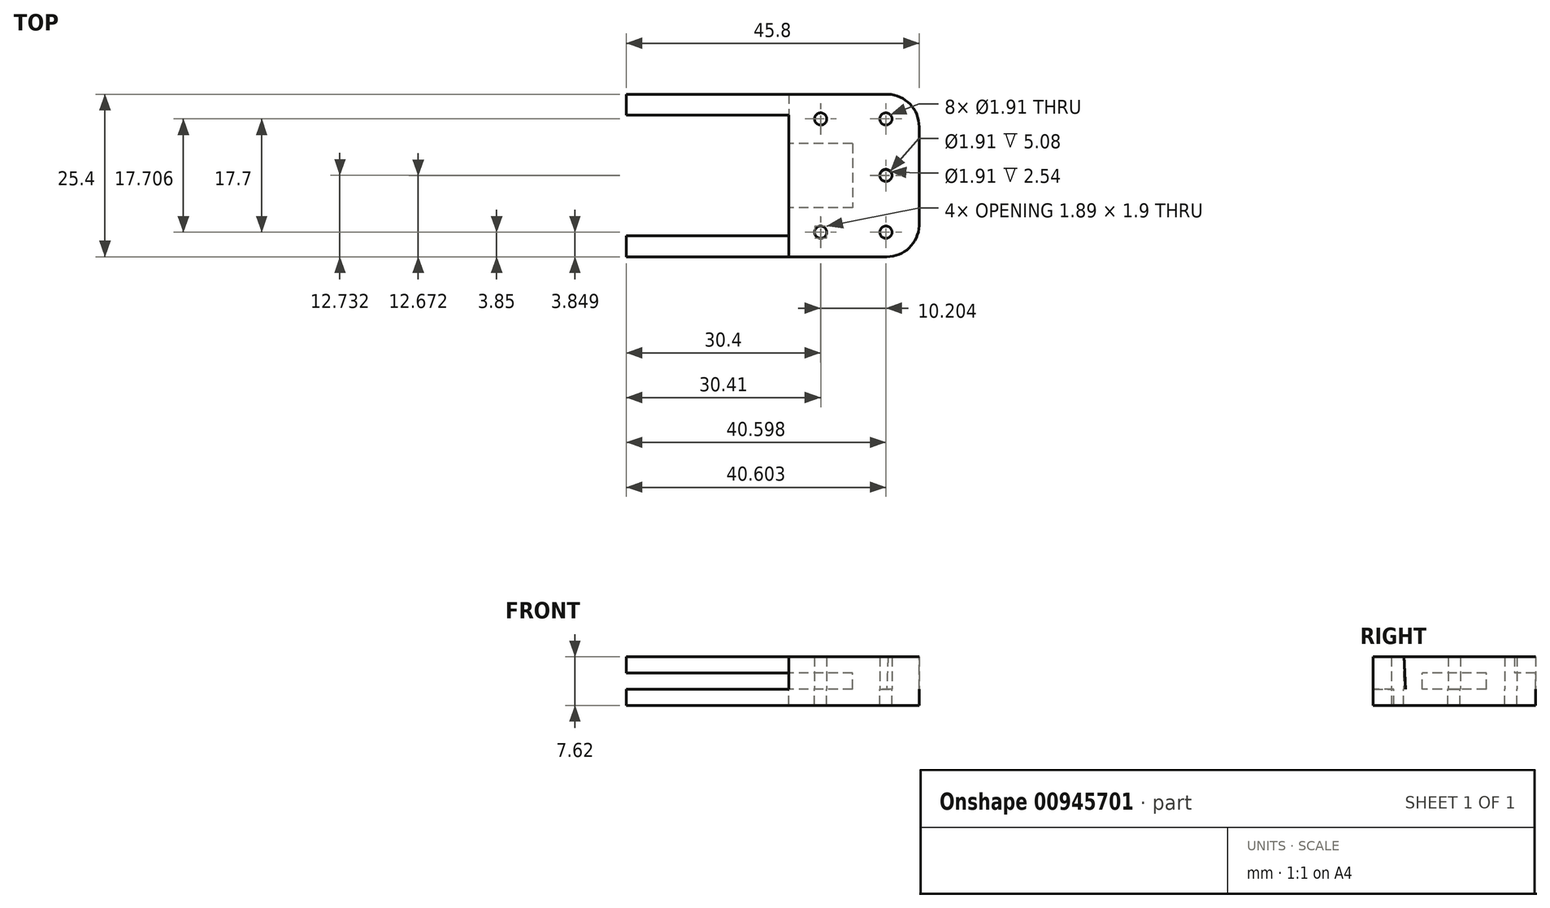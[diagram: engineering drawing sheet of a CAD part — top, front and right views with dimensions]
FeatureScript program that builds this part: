
annotation { "Feature Type Name" : "Feature", "Feature Type Description" : "" }
export const myFeature = defineFeature(function(context is Context, id is Id, definition is map)
    precondition{}
    {
        {
            var Q0;
            Q0=qCreatedBy(makeId("Top.planeOp"),FACE);
            var sketch = newSketch(context, id + "F0", { "sketchPlane" : qUnion([Q0])});
            skLineSegment(sketch, "E0.bottom", {"start": v(0, 0) * mm, "end": v(20.4, 0) * mm});
            skLineSegment(sketch, "E0.top", {"start": v(0, -25.4) * mm, "end": v(20.4, -25.4) * mm});
            skLineSegment(sketch, "E0.left", {"start": v(0, 0) * mm, "end": v(0, -25.4) * mm});
            skLineSegment(sketch, "E0.right", {"start": v(20.4, 0) * mm, "end": v(20.4, -25.4) * mm});
            skLineSegment(sketch, "E1.bottom", {"start": v(0, 0) * mm, "end": v(-25.4, 0) * mm});
            skLineSegment(sketch, "E1.top", {"start": v(0, -3.27) * mm, "end": v(-25.4, -3.27) * mm});
            skLineSegment(sketch, "E1.left", {"start": v(0, 0) * mm, "end": v(0, -3.27) * mm});
            skLineSegment(sketch, "E1.right", {"start": v(-25.4, 0) * mm, "end": v(-25.4, -3.27) * mm});
            skLineSegment(sketch, "E2.bottom", {"start": v(0, -7.7) * mm, "end": v(10, -7.7) * mm});
            skLineSegment(sketch, "E2.top", {"start": v(0, -17.7) * mm, "end": v(10, -17.7) * mm});
            skLineSegment(sketch, "E2.right", {"start": v(10, -7.7) * mm, "end": v(10, -17.7) * mm});
            skCircle(sketch, "E3", {"center": v(5, -3.85) * mm, "radius": 0.95 * mm});
            skCircle(sketch, "E4", {"center": v(15.2, -3.85) * mm, "radius": 0.95 * mm});
            skCircle(sketch, "E5", {"center": v(15.2, -21.55) * mm, "radius": 0.95 * mm});
            skCircle(sketch, "E6", {"center": v(5, -21.55) * mm, "radius": 0.95 * mm});
            skCircle(sketch, "E7", {"center": v(15.2, -12.67) * mm, "radius": 0.95 * mm});
            skSolve(sketch);
        }
        {
            var Q0;
            Q0=makeQuery(id+"F0.imprint","IMPRINT",FACE,{"disambiguationData":[TD([[makeQuery(id+"F0.imprint","IMPRINT",EDGE,{"derivedFrom":sQuery(id+"F0.wireOp",EDGE,"E1.bottom")}),1.0]])]});
            var Q1;
            Q1=makeQuery(id+"F0.imprint","IMPRINT",FACE,{"disambiguationData":[TD([[makeQuery(id+"F0.imprint","IMPRINT",EDGE,{"derivedFrom":sQuery(id+"F0.wireOp",EDGE,"E2.bottom")}),-1.0]])]});
            var Q2;
            Q2=makeQuery(id+"F0.imprint","IMPRINT",FACE,{"disambiguationData":[TD([[makeQuery(id+"F0.imprint","IMPRINT",EDGE,{"derivedFrom":sQuery(id+"F0.wireOp",EDGE,"E0.bottom")}),-1.0]])]});
            extrude(context, id + "F1", {"entities" : qUnion([Q0, Q1, Q2]), "depth" : 2.54 * mm, "offsetDistance" : 25.4 * mm});
        }
        {
            var Q0;
            Q0=qCreatedBy(makeId("Top.planeOp"),FACE);
            var sketch = newSketch(context, id + "F2", { "sketchPlane" : qUnion([Q0])});
            skLineSegment(sketch, "E8.bottom", {"start": v(0, 0) * mm, "end": v(20.4, 0) * mm});
            skLineSegment(sketch, "E8.top", {"start": v(0, -25.4) * mm, "end": v(20.4, -25.4) * mm});
            skLineSegment(sketch, "E8.right", {"start": v(20.4, 0) * mm, "end": v(20.4, -25.4) * mm});
            skLineSegment(sketch, "E9.bottom", {"start": v(10, -7.7) * mm, "end": v(0, -7.7) * mm});
            skLineSegment(sketch, "E9.top", {"start": v(10, -17.7) * mm, "end": v(0, -17.7) * mm});
            skLineSegment(sketch, "E9.left", {"start": v(10, -7.7) * mm, "end": v(10, -17.7) * mm});
            skLineSegment(sketch, "E10", {"start": v(0, 0) * mm, "end": v(0, -7.7) * mm});
            skLineSegment(sketch, "E11", {"start": v(0, -25.4) * mm, "end": v(0, -17.7) * mm});
            skCircle(sketch, "E12", {"center": v(5, -3.85) * mm, "radius": 0.95 * mm});
            skCircle(sketch, "E13", {"center": v(15.2, -3.85) * mm, "radius": 0.95 * mm});
            skCircle(sketch, "E14", {"center": v(15.2, -21.55) * mm, "radius": 0.95 * mm});
            skCircle(sketch, "E15", {"center": v(5, -21.55) * mm, "radius": 0.95 * mm});
            skCircle(sketch, "E16", {"center": v(15.2, -12.67) * mm, "radius": 0.95 * mm});
            skSolve(sketch);
        }
        {
            var Q0;
            Q0 = qSketchRegion(id + "F2", true);
            extrude(context, id + "F3", {"entities" : qUnion([Q0]), "operationType" : NewBodyOperationType.ADD, "oppositeDirection" : true, "depth" : 2.54 * mm, "offsetDistance" : 25.4 * mm});
        }
        {
            var Q0;
            Q0=makeQuery(id+"F3.boolean.opBoolean","MERGE",EDGE,{"derivedFrom":[makeQuery(id+"F1.opExtrude","SWEPT_EDGE",EDGE,{"disambiguationData":[OSD([sQuery(id+"F0.wireOp",EDGE,"E0.top"),sQuery(id+"F0.wireOp",EDGE,"E0.right")])]}),makeQuery(id+"F3.opExtrude","SWEPT_EDGE",EDGE,{"disambiguationData":[OSD([sQuery(id+"F2.wireOp",EDGE,"E8.top"),sQuery(id+"F2.wireOp",EDGE,"E8.right")])]})]});
            var Q1;
            Q1=makeQuery(id+"F3.boolean.opBoolean","MERGE",EDGE,{"derivedFrom":[makeQuery(id+"F1.opExtrude","SWEPT_EDGE",EDGE,{"disambiguationData":[OSD([sQuery(id+"F0.wireOp",EDGE,"E0.bottom"),sQuery(id+"F0.wireOp",EDGE,"E0.right")])]}),makeQuery(id+"F3.opExtrude","SWEPT_EDGE",EDGE,{"disambiguationData":[OSD([sQuery(id+"F2.wireOp",EDGE,"E8.bottom"),sQuery(id+"F2.wireOp",EDGE,"E8.right")])]})]});
            fillet(context, id + "F4", {"entities" : qUnion([Q0, Q1]), "radius" : 2.54 * mm, "tangentPropagation" : true, "allowEdgeOverflow" : false});
        }
        {
            var Q0;
            Q0=makeQuery(id+"F3.opExtrude","CAP_FACE",FACE,{"disambiguationData":[OSD([sQuery(id+"F2.wireOp",EDGE,"E8.bottom"),sQuery(id+"F2.wireOp",EDGE,"E8.top"),sQuery(id+"F2.wireOp",EDGE,"E8.right"),sQuery(id+"F2.wireOp",EDGE,"E9.bottom"),sQuery(id+"F2.wireOp",EDGE,"E9.top"),sQuery(id+"F2.wireOp",EDGE,"E9.left"),sQuery(id+"F2.wireOp",EDGE,"E10"),sQuery(id+"F2.wireOp",EDGE,"E11"),sQuery(id+"F2.wireOp",EDGE,"E12"),sQuery(id+"F2.wireOp",EDGE,"E13"),sQuery(id+"F2.wireOp",EDGE,"E14"),sQuery(id+"F2.wireOp",EDGE,"E15"),sQuery(id+"F2.wireOp",EDGE,"E16")])],"isStart":false});
            var sketch = newSketch(context, id + "F5", { "sketchPlane" : qUnion([Q0])});
            skLineSegment(sketch, "E17.bottom", {"start": v(0, 25.4) * mm, "end": v(20.4, 25.4) * mm});
            skLineSegment(sketch, "E17.top", {"start": v(0, 0) * mm, "end": v(20.4, 0) * mm});
            skLineSegment(sketch, "E17.left", {"start": v(0, 25.4) * mm, "end": v(0, 0) * mm});
            skLineSegment(sketch, "E17.right", {"start": v(20.4, 25.4) * mm, "end": v(20.4, 0) * mm});
            skLineSegment(sketch, "E18.bottom", {"start": v(0, 25.4) * mm, "end": v(-25.4, 25.4) * mm});
            skLineSegment(sketch, "E18.top", {"start": v(0, 22.12) * mm, "end": v(-25.4, 22.12) * mm});
            skLineSegment(sketch, "E18.left", {"start": v(0, 25.4) * mm, "end": v(0, 22.12) * mm});
            skLineSegment(sketch, "E18.right", {"start": v(-25.4, 25.4) * mm, "end": v(-25.4, 22.12) * mm});
            skLineSegment(sketch, "E19.bottom", {"start": v(0, 17.7) * mm, "end": v(10, 17.7) * mm});
            skLineSegment(sketch, "E19.top", {"start": v(0, 7.7) * mm, "end": v(10, 7.7) * mm});
            skLineSegment(sketch, "E19.right", {"start": v(10, 17.7) * mm, "end": v(10, 7.7) * mm});
            skCircle(sketch, "E20", {"center": v(5, 21.55) * mm, "radius": 0.95 * mm});
            skCircle(sketch, "E21", {"center": v(15.2, 21.55) * mm, "radius": 0.95 * mm});
            skCircle(sketch, "E22", {"center": v(15.2, 3.85) * mm, "radius": 0.95 * mm});
            skCircle(sketch, "E23", {"center": v(5, 3.85) * mm, "radius": 0.95 * mm});
            skCircle(sketch, "E24", {"center": v(15.2, 12.73) * mm, "radius": 0.95 * mm});
            skSolve(sketch);
        }
        {
            var Q0;
            Q0 = qSketchRegion(id + "F5", true);
            extrude(context, id + "F6", {"entities" : qUnion([Q0]), "operationType" : NewBodyOperationType.ADD, "depth" : 2.54 * mm, "offsetDistance" : 25.4 * mm});
        }
        {
            var Q0;
            Q0=makeQuery(id+"F6.opExtrude","SWEPT_EDGE",EDGE,{"disambiguationData":[OSD([sQuery(id+"F5.wireOp",EDGE,"E17.bottom"),sQuery(id+"F5.wireOp",EDGE,"E17.right")])]});
            var Q1;
            Q1=makeQuery(id+"F6.opExtrude","SWEPT_EDGE",EDGE,{"disambiguationData":[OSD([sQuery(id+"F5.wireOp",EDGE,"E17.top"),sQuery(id+"F5.wireOp",EDGE,"E17.right")])]});
            fillet(context, id + "F7", {"entities" : qUnion([Q0, Q1]), "radius" : 5.08 * mm, "tangentPropagation" : true, "allowEdgeOverflow" : false});
        }
    });
